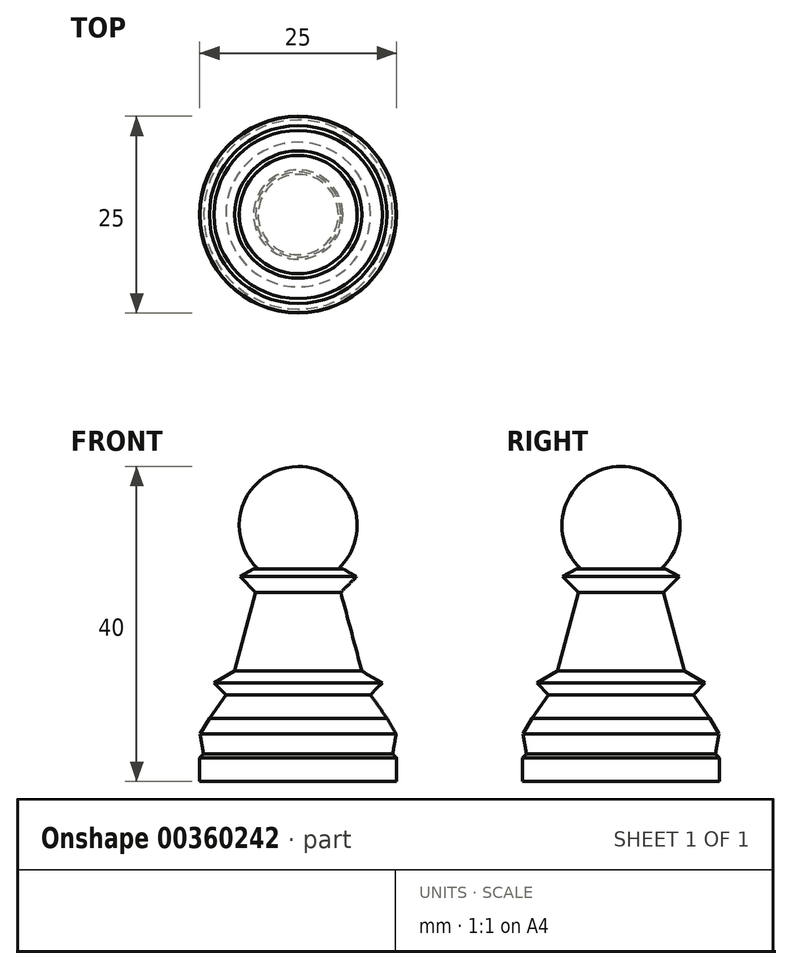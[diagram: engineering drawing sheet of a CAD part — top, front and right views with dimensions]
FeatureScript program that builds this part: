
annotation { "Feature Type Name" : "Feature", "Feature Type Description" : "" }
export const myFeature = defineFeature(function(context is Context, id is Id, definition is map)
    precondition{}
    {
        {
            var Q0;
            Q0=qCreatedBy(makeId("Top.planeOp"),FACE);
            var sketch = newSketch(context, id + "F0", { "sketchPlane" : qUnion([Q0])});
            skCircle(sketch, "E0", {"center": v(0, 0) * mm, "radius": 12.5 * mm});
            skSolve(sketch);
        }
        {
            var Q0;
            Q0=makeQuery(id+"F0.imprint","IMPRINT",FACE,{"disambiguationData":[TD([[makeQuery(id+"F0.imprint","IMPRINT",EDGE,{"derivedFrom":sQuery(id+"F0.wireOp",EDGE,"E0")}),1.0]])]});
            extrude(context, id + "F1", {"entities" : qUnion([Q0]), "depth" : 3 * mm});
        }
        {
            var Q0;
            Q0=makeQuery(id+"F1.opExtrude","CAP_FACE",FACE,{"disambiguationData":[OSD([sQuery(id+"F0.wireOp",EDGE,"E0")])],"isStart":false});
            var Q1;
            Q1=makeQuery(id+"F1.opExtrude","CAP_FACE",FACE,{"disambiguationData":[OSD([sQuery(id+"F0.wireOp",EDGE,"E0")])],"isStart":true});
            extrude(context, id + "F2", {"entities" : qUnion([Q0, Q1]), "operationType" : NewBodyOperationType.ADD, "depth" : .5 * mm, "hasDraft" : true, "draftAngle" : 45 * degree, "draftPullDirection" : true});
        }
        {
            var Q0;
            {var subQ0=sQuery(id+"F0.wireOp",EDGE,"E0");Q0=makeQuery(id+"F2.opExtrude","CAP_FACE",FACE,{"disambiguationData":[OSD([subQ0]),TDD([makeQuery(id+"F1.opExtrude","CAP_FACE",FACE,{"disambiguationData":[OSD([subQ0])],"isStart":false})])],"isStart":false});}
            extrude(context, id + "F3", {"entities" : qUnion([Q0]), "depth" : 2.5 * mm, "hasDraft" : true, "draftAngle" : 10 * degree});
        }
        {
            var Q0;
            Q0=makeQuery(id+"F3.opExtrude","CAP_FACE",FACE,{"disambiguationData":[OSD([sQuery(id+"F0.wireOp",EDGE,"E0")])],"isStart":false});
            extrude(context, id + "F4", {"entities" : qUnion([Q0]), "operationType" : NewBodyOperationType.ADD, "depth" : 2 * mm, "hasDraft" : true, "draftAngle" : 30 * degree, "draftPullDirection" : true});
        }
        {
            var Q0;
            Q0=makeQuery(id+"F4.opExtrude","CAP_FACE",FACE,{"disambiguationData":[OSD([sQuery(id+"F0.wireOp",EDGE,"E0")])],"isStart":false});
            extrude(context, id + "F5", {"entities" : qUnion([Q0]), "operationType" : NewBodyOperationType.ADD, "depth" : 3 * mm, "hasDraft" : true, "draftAngle" : 35 * degree, "draftPullDirection" : true});
        }
        {
            var Q0;
            Q0=makeQuery(id+"F5.opExtrude","CAP_FACE",FACE,{"disambiguationData":[OSD([sQuery(id+"F0.wireOp",EDGE,"E0")])],"isStart":false});
            extrude(context, id + "F6", {"entities" : qUnion([Q0]), "operationType" : NewBodyOperationType.ADD, "depth" : 1.5 * mm, "hasDraft" : true, "draftAngle" : 45 * degree});
        }
        {
            var Q0;
            Q0=makeQuery(id+"F6.opExtrude","CAP_FACE",FACE,{"disambiguationData":[OSD([sQuery(id+"F0.wireOp",EDGE,"E0")])],"isStart":false});
            extrude(context, id + "F7", {"entities" : qUnion([Q0]), "operationType" : NewBodyOperationType.ADD, "depth" : 1.5 * mm, "hasDraft" : true, "draftAngle" : 60 * degree, "draftPullDirection" : true});
        }
        {
            var Q0;
            Q0=makeQuery(id+"F7.opExtrude","CAP_FACE",FACE,{"disambiguationData":[OSD([sQuery(id+"F0.wireOp",EDGE,"E0")])],"isStart":false});
            extrude(context, id + "F8", {"entities" : qUnion([Q0]), "operationType" : NewBodyOperationType.ADD, "depth" : 10 * mm, "hasDraft" : true, "draftAngle" : 15 * degree, "draftPullDirection" : true});
        }
        {
            var Q0;
            Q0=makeQuery(id+"F8.opExtrude","CAP_FACE",FACE,{"disambiguationData":[OSD([sQuery(id+"F0.wireOp",EDGE,"E0")])],"isStart":false});
            extrude(context, id + "F9", {"entities" : qUnion([Q0]), "operationType" : NewBodyOperationType.ADD, "depth" : 2 * mm, "hasDraft" : true, "draftAngle" : 45 * degree});
        }
        {
            var Q0;
            Q0=makeQuery(id+"F9.opExtrude","CAP_FACE",FACE,{"disambiguationData":[OSD([sQuery(id+"F0.wireOp",EDGE,"E0")])],"isStart":false});
            extrude(context, id + "F10", {"entities" : qUnion([Q0]), "operationType" : NewBodyOperationType.ADD, "depth" : 1 * mm, "hasDraft" : true, "draftAngle" : 60 * degree, "draftPullDirection" : true});
        }
        {
            var Q0;
            Q0=qCreatedBy(makeId("Front.planeOp"),FACE);
            var sketch = newSketch(context, id + "F11", { "sketchPlane" : qUnion([Q0])});
            skLineSegment(sketch, "E1", {"start": v(0, 0) * mm, "end": v(0, 49.8) * mm});
            skCircle(sketch, "E2", {"center": v(0, 32.5) * mm, "radius": 7.5 * mm});
            skSolve(sketch);
        }
        {
            var Q0;
            {var subQ0=sQuery(id+"F11.wireOp",EDGE,"E2");var subQ1=sQuery(id+"F11.wireOp",EDGE,"E1");var subQ2=makeQuery(id+"F11.imprint","INTERSECT",VERTEX,{"disambiguationData":[OD(0.0)],"derivedFrom":[subQ1,subQ0]});Q0=makeQuery(id+"F11.imprint","IMPRINT",FACE,{"disambiguationData":[TD([[makeQuery(id+"F11.imprint","IMPRINT",EDGE,{"disambiguationData":[TD([[subQ2,-1.0]])],"derivedFrom":subQ1}),-1.0]])]});}
            var Q1;
            Q1=sQuery(id+"F11.wireOp",EDGE,"E1");
            revolve(context, id + "F12", {"operationType" : NewBodyOperationType.ADD, "entities" : qUnion([Q0]), "axis" : qUnion([Q1]), "revolveType" : RevolveType.FULL});
        }
    });
